# Revit family: led_p_t8_glass_600_8w_100pct_3000k_ct_140062610
name_source: partatom
category: Leuchten
revit_build: Autodesk Revit 2016 (Build: 20190508_0715(x64)
units: mm (PartAtom-declared; Revit-internal decimal feet)

## family parameters
Basisbauteil = Fläche
Beim Laden mit Abzugskörper schneiden = Nein
Bemaßung runder Anschluss = Durchmesser verwenden
Gemeinsam genutzt = Nein
Lichtquelle = Nein
Raumberechnungspunkt = Nein
Teiletyp = Normal

## types (1)
- LED P T8 glass 600 8W 100pct 3000K CT (1 x LED, 1050 lm)
    Approval mark = CE
    Beschreibung = Single-ended full IEC compliant LED Tube with patented driver and full glass body. Retrofit existing T8 lamps with EM ballast installations ONLY!. No warm-up time, 100% light instantly when switched on. Full glass. Up to 62% lower energy consumption than fluorescent.
    CIE Flux Codes = 35 63 84 79 102
    Height = 26 mm  [stored 0.0853018 ft]
    Hersteller = OPPLE
    Lamp Light Flux = 1050 lm
    Lamp count = 1
    Lampe = 1 x LED
    Length = 604 mm
    Luminous efficacy = 133 lm/W
    ModVariant = Nein
    Modell = 140062610
    Mounting Place = Ceiling
    Mounting Type = Surface mounted
    Number of Poles = 1
    OnlyDefault = Ja
    Power Factor = 1
    Product Name = LED P T8 glass 600 8W 100pct 3000K CT
    Product group = T8 Tube
    ProductGroupID = 340
    Protection Class = Protection class I
    Protection Degree = IP 20
    RLX_Detail_Level = 1
    RlxData = <blob elided: 22393 chars, md5=e51e4bc7>
    Scheinlast = 8 VA
    Socket = socket
    Standby Power = 0 W
    System Light Flux = 1067 lm
    System Power = 8 W
    Typenbild = 140062610.jpg
    Typenkommentare = Product without accessories
    URL = http://relux.com
    VarID = ---
    Voltage = 0 V
    Vorgabe-Ansicht = 1800 mm
    Weight = 0.00 kg
    Width = 26 mm  [stored 0.0853018 ft]

note: [stored X ft] marks values corroborated as IEEE doubles in the binary element streams (Revit-internal decimal feet)

## geometry (parser evidence)
native form markers: Blend x4, Sweep x13
no freeform markers — native parametric forms only
